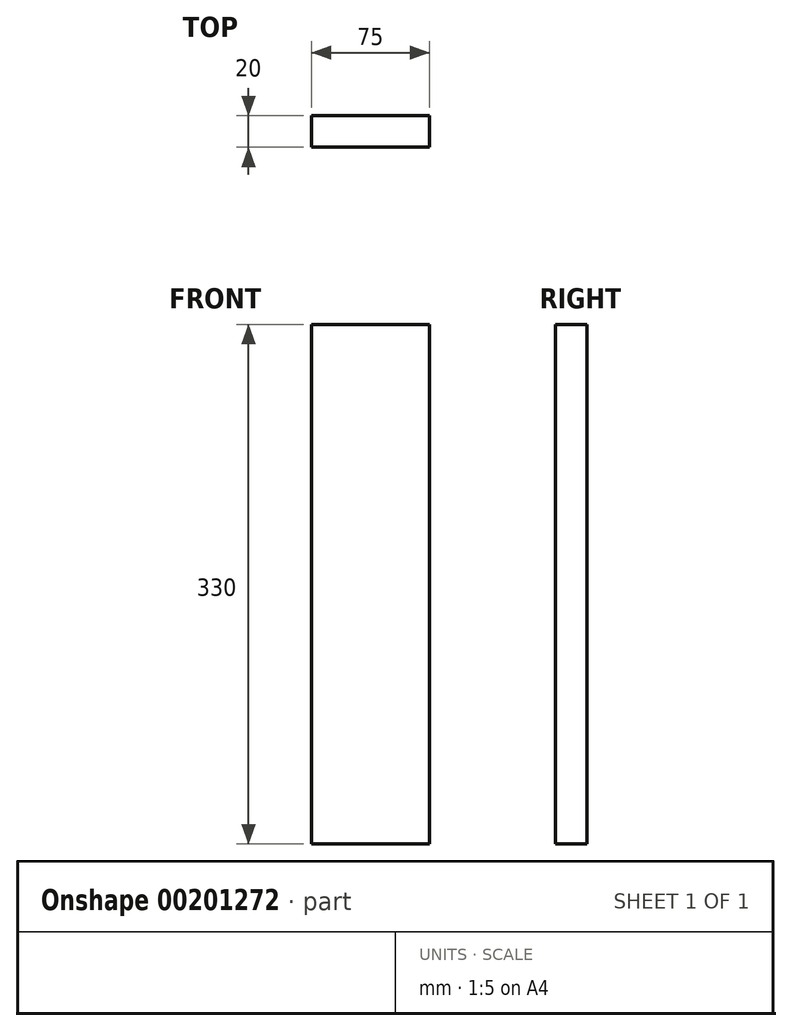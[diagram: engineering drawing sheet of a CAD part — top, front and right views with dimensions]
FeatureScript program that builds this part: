
annotation { "Feature Type Name" : "Feature", "Feature Type Description" : "" }
export const myFeature = defineFeature(function(context is Context, id is Id, definition is map)
    precondition{}
    {
        {
            var Q0;
            Q0=qCreatedBy(makeId("Top.planeOp"),FACE);
            var sketch = newSketch(context, id + "F0", { "sketchPlane" : qUnion([Q0])});
            skLineSegment(sketch, "E0.bottom", {"start": v(0, 0) * mm, "end": v(75, 0) * mm});
            skLineSegment(sketch, "E0.top", {"start": v(0, 20) * mm, "end": v(75, 20) * mm});
            skLineSegment(sketch, "E0.left", {"start": v(0, 0) * mm, "end": v(0, 20) * mm});
            skLineSegment(sketch, "E0.right", {"start": v(75, 0) * mm, "end": v(75, 20) * mm});
            skSolve(sketch);
        }
        {
            var Q0;
            Q0 = qSketchRegion(id + "F0", true);
            extrude(context, id + "F1", {"entities" : qUnion([Q0]), "depth" : 330 * mm});
        }
    });
